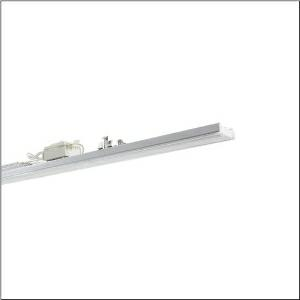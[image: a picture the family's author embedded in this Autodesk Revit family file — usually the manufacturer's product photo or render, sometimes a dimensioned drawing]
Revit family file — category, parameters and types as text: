
# Revit family: licross_21_recessed_mo_51te11vn465g
name_source: partatom
category: Lighting Fixtures
units: mm (PartAtom-declared; Revit-internal decimal feet)

## family parameters
Cut with Voids When Loaded = No
Host = Face
Light Source = No
Part Type = Normal
Room Calculation Point = No
Round Connector Dimension = Use Diameter
Shared = No

## types (1)
- --- (1 x LED, 6500 lm, 34.8 W, 4000K)
    Apparent Load = 35 VA
    CIE Flux Codes = 89 96 99 100 100
    Color Rendering = 80
    Color Temperature = 4000K
    Default Elevation = 1800 mm
    Description = Licross 21 Recessed MO, luminaire insert, of sheet steel, galvanised, coil coated, white, length: 1.500mm, width: 66mm, height: 67mm, LED rated luminous flux: 6.500lm, light colour: 840, SDCM (Standard Deviation of Colour Matching)MacAdam ≤ 2 SDCM (initial), control gear: DALI 2, CLO, with plug, 5-pole, with phase selection, mains connection: 220..240V, AC, 50/60Hz, start of lifetime: 35W, end of service life: 38W, internal wiring halogen-free, primary light control with lens, of plastic, primary optical cover: cover, of PMMA, light emission: direct distribution, primary light characteristic: symmetric, protection rating (complete): IP54, insulation class (complete): insulation class I (protective earthing), certification: CE, ENEC, VDE, UKCA, protection symbol: D if used in an environment with non-conductive dust loads with corresponding accessories, impact resistance: IK06, permissible ambient temperature for indoor applications: -25..+40°C, corresponds to IFS (International Featured Standards) requirements for safety and quality in the food industry, reducing of maximum allowable ambient temperature of 5°C with ceiling mounting, LABS conformity tested according to VDMA 24364:2018-05, The light source and the operating device comply with the requirements of the Ecodesign Regulation (EU) 2019/2020 and are replaceable in accordance with this regulation, packaging unit: 1 piece
    Height = 58 mm
    Lamp = 1 x LED
    Lamp Light Flux = 6500 lm
    Lamp Power = 34.8 W
    Lamp count = 1
    Length = 1500 mm
    Luminous efficacy = 187 lm/W
    Manufacturer = Siteco
    ModVariant = No
    Model = 51TE11VN465G
    Mounting Place = Ceiling
    Mounting Type = Pendant
    Number of Poles = 1
    OnlyDefault = Yes
    Power Factor = 1
    Product Name = Licross 21 Recessed MO
    Product group = luminaire insert | ceiling pendant
    ProductGroupID = 901
    Protection Class = Protection class I
    Protection Degree = IP 54
    RLX_Detail_Level = 1
    RLX_Emergency_Light_Flux = 0 lm
    RLX_Emergency_Type = 0
    RLX_Emergency_Type_DB = No
    RlxData = <blob elided: 24649 chars, md5=c42fe3cd>
    Socket = socket
    Standby Power = 0 W
    System Light Flux = 6500 lm
    System Power = 35 W
    Type Comments = factory setting: luminous flux: 100 % | dim-lin: 254 | 236 mA
    Type Image = l_1296930.jpg
    URL = http://relux.com
    VarID = @adj_092279
    Voltage = 0 V
    Weight = 0.00 kg
    Width = 66 mm

## geometry (parser evidence)
native form markers: Blend x4, Sweep x12
no freeform markers — native parametric forms only
